# Revit family: 2021687 Sylvania Lighting Fixture OPTIX R 1200 ASYMMETRIC 4K SSC WHITE
name_source: partatom
category: Lighting Fixtures
revit_build: Autodesk Revit 2018 (Build: 20170223_1515(x64)
units: mm (PartAtom-declared; Revit-internal decimal feet)

## family parameters
Cut with Voids When Loaded = No
Host = Face
Light Source = Yes
OmniClass Number = 23.80.70.00
OmniClass Title = Lighting
Part Type = Normal
Room Calculation Point = No
Round Connector Dimension = Use Diameter
Shared = No

## types (1)
- 2021687 OPTIX R 1200 ASYM 4K SSC WHT
    Apparent Load = 31 VA
    Assembly Code = D5020200
    AssetType = Fixed
    ClassificationName = Uniclass2015
    ClassificationValue = EF_70_80
    Color Filter = 16777215
    Cost = 0 $
    Default Elevation = 1219 mm
    Description = Recessed LED Linear luminaire with Asymmetric Aluminium Reflector, Asymmetric Light Distribution, Luminaire Dimensions: 1196x293x52mm, Sylvania White body colour, IP20, IK07, SylSmart Standalone Office controlled, Low LED flicker (+/-5%), Warm White (3000K) LED Colour Temperature, 3480lm, 31W, 112lm/W efficacy, CRI>80, 3 SDCM (3-step MacAdam ellipse) LED Colour Consistency, Lumen Maintenance: L90B50 at 60,000 hours.
    Dimming Lamp Color Temperature Shift = <None>
    DocumentationLiterature = http://www.sylvania-lighting.com
    DurationUnit = hours
    ElectricShockClassification = 112
    Emit Shape Visible in Rendering = No
    Emit from Circle Diameter = 610 mm
    ExpectedLife = 50000
    Height = 52 mm
    IfcExportAs = Class I
    IfcExportType = IfcLightFixtureType
    ImpactProtectionIndex = IfcLightFixtureType
    IngressProtection = IfcLightFixtureType
    InputNominalFrequency = 4000
    InputVoltage = 0
    LampColourRenderingIndex = 16500
    LampColourTemperature = LED
    LampMacAdamStep = 80
    LampNominalLuminous = 4000 K
    Length = 1196 mm  [stored 3.92388 ft]
    LightOutputRatio = LED
    LuminaireType = 0
    ManufacturerName = 112 lm/W
    Material = Feilo Sylvania
    Material_1_FEILO = <By Category>
    Material_2_FEILO = <By Category>
    Material_3_FEILO = <By Category>
    Material_4_FEILO = <By Category>
    Model = OPTIX R 1200 ASYMMETRIC 4K SSC WHITE
    ModelNumber = 2021687
    ModelReference = OPTIX R 1200 ASYMMETRIC 4K SSC WHITE
    Name = OPTIX R 1200 ASYMMETRIC 4K SSC WHITE
    NominalDepth = 0 mm  [stored 0 ft]
    NominalHeight = 0 mm  [stored 0 ft]
    NominalLength = 293 mm
    Photometric Web File = 2021687.ies
    PowerConsumption = Lighting
    PowerFactor = 0
    Tilt Angle = 90.00°
    Type Image = <None>
    TypeName = OPTIX R 1200 ASYMMETRIC 4K SSC WHITE
    URL = 1
    Voltage = 0 V
    WarrantyDescription = http://www.sylvania-lighting.com
    Width = 293 mm
    spacer centres = 1000 mm  [stored 3.28084 ft]
    spacer height = 8 mm  [stored 0.0262467 ft]

note: [stored X ft] marks values corroborated as IEEE doubles in the binary element streams (Revit-internal decimal feet)

## geometry (parser evidence)
native form markers: Sweep x2
no freeform markers — native parametric forms only
